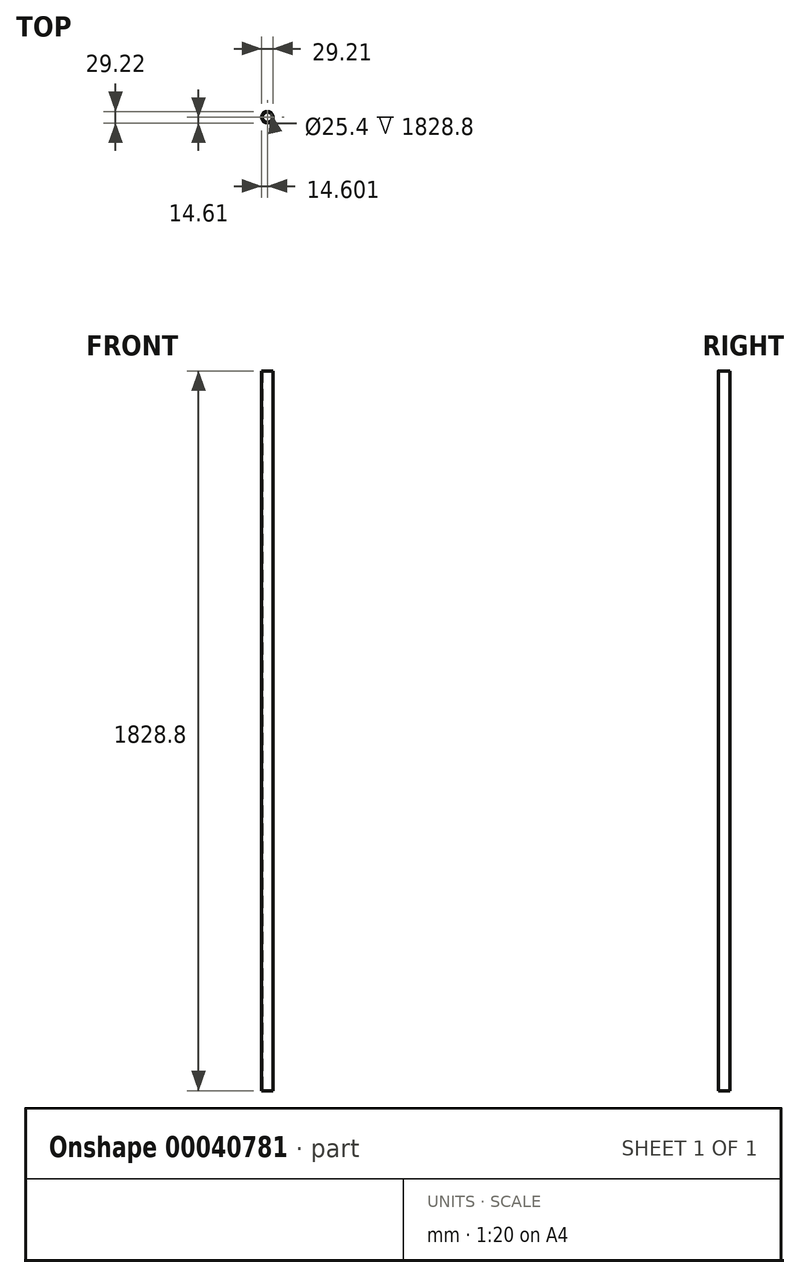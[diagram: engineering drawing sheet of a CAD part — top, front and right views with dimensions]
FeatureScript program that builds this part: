
annotation { "Feature Type Name" : "Feature", "Feature Type Description" : "" }
export const myFeature = defineFeature(function(context is Context, id is Id, definition is map)
    precondition{}
    {
        {
            var Q0;
            Q0=qCreatedBy(makeId("Top.planeOp"),FACE);
            var sketch = newSketch(context, id + "F0", { "sketchPlane" : qUnion([Q0])});
            skCircle(sketch, "E0", {"center": v(2.52, 0) * mm, "radius": 14.6 * mm});
            skCircle(sketch, "E1", {"center": v(2.52, 0) * mm, "radius": 12.7 * mm});
            skSolve(sketch);
        }
        {
            var Q0;
            Q0=makeQuery(id+"F0.imprint","IMPRINT",FACE,{"disambiguationData":[TD([[makeQuery(id+"F0.imprint","IMPRINT",EDGE,{"derivedFrom":sQuery(id+"F0.wireOp",EDGE,"E0")}),1.0]])]});
            extrude(context, id + "F1", {"entities" : qUnion([Q0]), "depth" : 1828.8 * mm});
        }
    });
